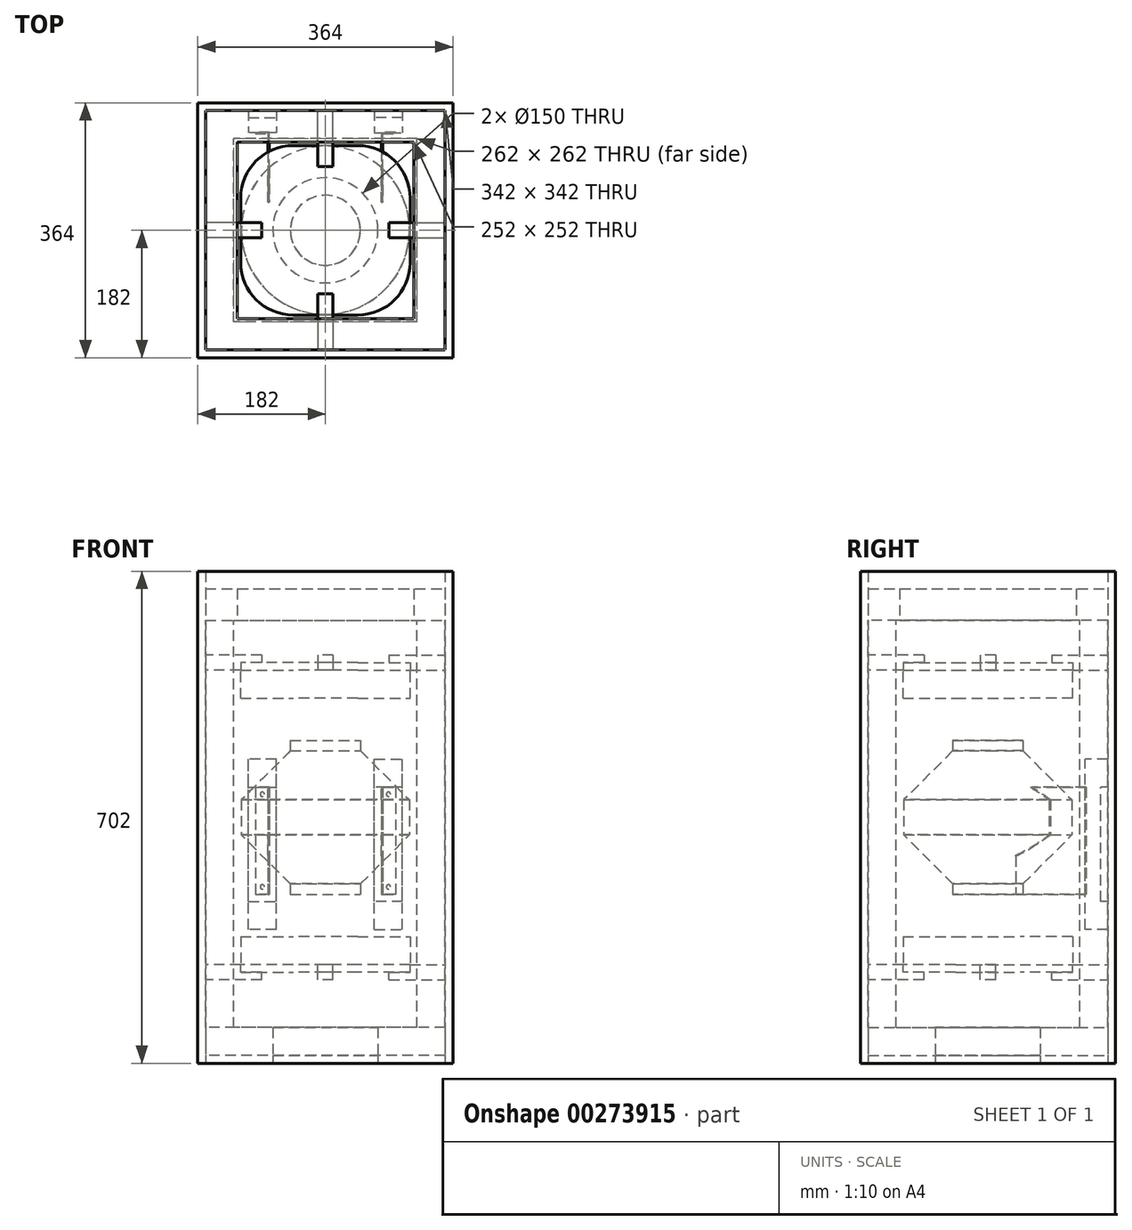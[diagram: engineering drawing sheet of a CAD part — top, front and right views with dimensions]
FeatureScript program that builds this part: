
annotation { "Feature Type Name" : "Feature", "Feature Type Description" : "" }
export const myFeature = defineFeature(function(context is Context, id is Id, definition is map)
    precondition{}
    {
        {
            assignVariable(context, id + "F0", {"variableType" : VariableType.LENGTH, "name" : "FanHeight", "lengthValue" : 220 * mm});
        }
        {
            assignVariable(context, id + "F1", {"variableType" : VariableType.LENGTH, "name" : "DistToPlate", "lengthValue" : 100 * mm});
        }
        {
            assignVariable(context, id + "F2", {"variableType" : VariableType.LENGTH, "name" : "InsulThickness", "lengthValue" : 40 * mm});
        }
        {
            var Q0;
            Q0=qCreatedBy(makeId("Front.planeOp"),FACE);
            var sketch = newSketch(context, id + "F3", { "sketchPlane" : qUnion([Q0])});
            skLineSegment(sketch, "E0", {"start": v(0, 110) * mm, "end": v(-50, 110) * mm});
            skLineSegment(sketch, "E1", {"start": v(-50, 110) * mm, "end": v(-50, 95) * mm});
            skLineSegment(sketch, "E2", {"start": v(-50, 95) * mm, "end": v(-120, 25) * mm});
            skLineSegment(sketch, "E3", {"start": v(-120, 25) * mm, "end": v(-120, -25) * mm});
            skLineSegment(sketch, "E4", {"start": v(-120, -25) * mm, "end": v(-50, -95) * mm});
            skLineSegment(sketch, "E5", {"start": v(-50, -95) * mm, "end": v(-50, -110) * mm});
            skLineSegment(sketch, "E6", {"start": v(-50, -110) * mm, "end": v(0, -110) * mm});
            skLineSegment(sketch, "E7", {"start": v(0, -110) * mm, "end": v(0, 110) * mm});
            skSolve(sketch);
        }
        {
            var Q0;
            Q0=qSketchRegion(id+"F3",true);
            var Q1;
            Q1=sQuery(id+"F3.wireOp",EDGE,"E7");
            revolve(context, id + "F4", {"surfaceOperationType" : NewSurfaceOperationType.NEW, "entities" : qUnion([Q0]), "axis" : qUnion([Q1]), "revolveType" : RevolveType.FULL});
        }
        {
            var Q0;
            Q0=qCreatedBy(makeId("Top.planeOp"),FACE);
            cPlane(context, id + "F5", {"entities" : qUnion([Q0]), "cplaneType" : CPlaneType.OFFSET, "offset" : (getVariable(context, 'FanHeight') / 2), "oppositeDirection" : true, "width" : 150 * mm, "height" : 150 * mm});
        }
        {
            var Q0;
            Q0=qCreatedBy(id+"F5.planeOp",FACE);
            var sketch = newSketch(context, id + "F6", { "sketchPlane" : qUnion([Q0])});
            skLineSegment(sketch, "E8", {"start": v(82, 40) * mm, "end": v(82, 138) * mm});
            skLineSegment(sketch, "E9", {"start": v(82, 138) * mm, "end": v(100, 138) * mm});
            skLineSegment(sketch, "E10", {"start": v(100, 138) * mm, "end": v(100, 140) * mm});
            skLineSegment(sketch, "E11", {"start": v(100, 140) * mm, "end": v(80, 140) * mm});
            skLineSegment(sketch, "E12", {"start": v(80, 140) * mm, "end": v(80, 40) * mm});
            skLineSegment(sketch, "E13", {"start": v(80, 40) * mm, "end": v(82, 40) * mm});
            skLineSegment(sketch, "E14", {"start": v(-80, 40) * mm, "end": v(-80, 140) * mm});
            skLineSegment(sketch, "E15", {"start": v(-80, 140) * mm, "end": v(-100, 140) * mm});
            skLineSegment(sketch, "E16", {"start": v(-100, 140) * mm, "end": v(-100, 138) * mm});
            skLineSegment(sketch, "E17", {"start": v(-100, 138) * mm, "end": v(-82, 138) * mm});
            skLineSegment(sketch, "E18", {"start": v(-82, 138) * mm, "end": v(-82, 40) * mm});
            skLineSegment(sketch, "E19", {"start": v(-82, 40) * mm, "end": v(-80, 40) * mm});
            skSolve(sketch);
        }
        {
            var Q0;
            Q0=qSketchRegion(id+"F6",true);
            extrude(context, id + "F7", {"entities" : qUnion([Q0]), "operationType" : NewBodyOperationType.ADD, "offsetDistance" : 25 * mm, "depth" : 153 * mm});
        }
        {
            var Q0;
            Q0=makeQuery(id+"F7.opExtrude","SWEPT_FACE",FACE,{"disambiguationData":[OSD([sQuery(id+"F6.wireOp",EDGE,"E11")])]});
            var sketch = newSketch(context, id + "F8", { "sketchPlane" : qUnion([Q0])});
            skCircle(sketch, "E20", {"center": v(-90, 33) * mm, "radius": 3 * mm});
            skCircle(sketch, "E21", {"center": v(-90, -99.22) * mm, "radius": 3 * mm});
            skCircle(sketch, "E22", {"center": v(90, -99.22) * mm, "radius": 3 * mm});
            skCircle(sketch, "E23", {"center": v(90, 33) * mm, "radius": 3 * mm});
            skLineSegment(sketch, "E24", {"start": v(-90, 43) * mm, "end": v(-90, -69.24) * mm, "construction": true});
            skPoint(sketch, "E24.endSnap0", {"position": v(-90, 43) * mm});
            skPoint(sketch, "E25", {"position": v(-90, -110) * mm});
            skSolve(sketch);
        }
        {
            var Q0;
            Q0=qSketchRegion(id+"F8",true);
            extrude(context, id + "F9", {"entities" : qUnion([Q0]), "operationType" : NewBodyOperationType.REMOVE, "oppositeDirection" : true, "offsetDistance" : 25 * mm, "depth" : 25 * mm});
        }
        {
            var Q0;
            Q0=makeQuery(id+"F7.opExtrude","SWEPT_FACE",FACE,{"disambiguationData":[OSD([sQuery(id+"F6.wireOp",EDGE,"E11")])]});
            var Q1;
            Q1=makeQuery(id+"F7.opExtrude","SWEPT_FACE",FACE,{"disambiguationData":[OSD([sQuery(id+"F6.wireOp",EDGE,"E9")])]});
            cPlane(context, id + "F10", {"entities" : qUnion([Q0, Q1]), "cplaneType" : CPlaneType.MID_PLANE, "offset" : 25 * mm, "width" : 150 * mm, "height" : 150 * mm});
        }
        {
            var Q0;
            Q0=qCreatedBy(id+"F10.planeOp",FACE);
            var sketch = newSketch(context, id + "F11", { "sketchPlane" : qUnion([Q0])});
            skCircle(sketch, "E26.0", {"center": v(-90, 33) * mm, "radius": 3 * mm, "construction": true});
            skLineSegment(sketch, "E27.bottom", {"start": v(-70, -160) * mm, "end": v(-110, -160) * mm});
            skLineSegment(sketch, "E27.top", {"start": v(-70, 83) * mm, "end": v(-110, 83) * mm});
            skLineSegment(sketch, "E27.left", {"start": v(-70, -160) * mm, "end": v(-70, 83) * mm});
            skLineSegment(sketch, "E27.right", {"start": v(-110, -160) * mm, "end": v(-110, 83) * mm});
            skPoint(sketch, "E27.middle", {"position": v(-90, -38.5) * mm});
            skSolve(sketch);
        }
        {
            var Q0;
            Q0 = qSketchRegion(id + "F11", true);
            extrude(context, id + "F12", {"entities" : qUnion([Q0]), "depth" : 22 * mm, "offsetDistance" : 25 * mm});
        }
        {
            var Q0;
            Q0=makeQuery(id+"F12.opExtrude","CAP_FACE",FACE,{"disambiguationData":[OSD([sQuery(id+"F11.wireOp",EDGE,"E27.bottom"),sQuery(id+"F11.wireOp",EDGE,"E27.top"),sQuery(id+"F11.wireOp",EDGE,"E27.left"),sQuery(id+"F11.wireOp",EDGE,"E27.right")])],"isStart":false});
            var sketch = newSketch(context, id + "F13", { "sketchPlane" : qUnion([Q0])});
            skLineSegment(sketch, "E28.bottom", {"start": v(-110, 83) * mm, "end": v(-70, 83) * mm});
            skLineSegment(sketch, "E28.top", {"start": v(-110, 43) * mm, "end": v(-70, 43) * mm});
            skLineSegment(sketch, "E28.left", {"start": v(-110, 83) * mm, "end": v(-110, 43) * mm});
            skLineSegment(sketch, "E28.right", {"start": v(-70, 83) * mm, "end": v(-70, 43) * mm});
            skLineSegment(sketch, "E29.bottom", {"start": v(-110, -160) * mm, "end": v(-70, -160) * mm});
            skLineSegment(sketch, "E29.top", {"start": v(-110, -120) * mm, "end": v(-70, -120) * mm});
            skLineSegment(sketch, "E29.left", {"start": v(-110, -160) * mm, "end": v(-110, -120) * mm});
            skLineSegment(sketch, "E29.right", {"start": v(-70, -160) * mm, "end": v(-70, -120) * mm});
            skSolve(sketch);
        }
        {
            var Q0;
            Q0 = qSketchRegion(id + "F13", true);
            extrude(context, id + "F14", {"entities" : qUnion([Q0]), "operationType" : NewBodyOperationType.ADD, "depth" : 10 * mm, "offsetDistance" : 25 * mm});
        }
        {
            var Q0;
            Q0=makeQuery(id+"F12.opExtrude","SWEPT_BODY",BODY,{"disambiguationData":[OSD([sQuery(id+"F11.wireOp",EDGE,"E27.bottom"),sQuery(id+"F11.wireOp",EDGE,"E27.top"),sQuery(id+"F11.wireOp",EDGE,"E27.left"),sQuery(id+"F11.wireOp",EDGE,"E27.right")])]});
            var Q1;
            Q1=qCreatedBy(makeId("Right.planeOp"),FACE);
            mirror(context, id + "F15", {"entities" : qUnion([Q0]), "mirrorPlane" : qUnion([Q1])});
        }
        {
            var Q0;
            Q0=qCreatedBy(makeId("Top.planeOp"),FACE);
            cPlane(context, id + "F16", {"entities" : qUnion([Q0]), "cplaneType" : CPlaneType.OFFSET, "offset" : (getVariable(context, 'FanHeight') / 2 + getVariable(context, 'DistToPlate')), "width" : 150 * mm, "height" : 150 * mm});
        }
        {
            var Q0;
            Q0=qCreatedBy(id+"F16.planeOp",FACE);
            var sketch = newSketch(context, id + "F17", { "sketchPlane" : qUnion([Q0])});
            skLineSegment(sketch, "E30.bottom", {"start": v(121, -121) * mm, "end": v(-121, -121) * mm});
            skLineSegment(sketch, "E30.top", {"start": v(121, 121) * mm, "end": v(-121, 121) * mm});
            skLineSegment(sketch, "E30.left", {"start": v(121, -121) * mm, "end": v(121, 121) * mm});
            skLineSegment(sketch, "E30.right", {"start": v(-121, -121) * mm, "end": v(-121, 121) * mm});
            skPoint(sketch, "E30.middle", {"position": v(0, 0) * mm});
            skSolve(sketch);
        }
        {
            var Q0;
            Q0 = qSketchRegion(id + "F17", true);
            extrude(context, id + "F18", {"entities" : qUnion([Q0]), "depth" : 11 * mm, "offsetDistance" : 25 * mm});
        }
        {
            var Q0;
            Q0=makeQuery(id+"F18.opExtrude","CAP_FACE",FACE,{"disambiguationData":[OSD([sQuery(id+"F17.wireOp",EDGE,"E30.bottom"),sQuery(id+"F17.wireOp",EDGE,"E30.top"),sQuery(id+"F17.wireOp",EDGE,"E30.left"),sQuery(id+"F17.wireOp",EDGE,"E30.right")])],"isStart":true});
            var sketch = newSketch(context, id + "F19", { "sketchPlane" : qUnion([Q0])});
            skLineSegment(sketch, "E31.bottom", {"start": v(171, -171) * mm, "end": v(-171, -171) * mm, "construction": true});
            skLineSegment(sketch, "E31.top", {"start": v(171, 171) * mm, "end": v(-171, 171) * mm, "construction": true});
            skLineSegment(sketch, "E31.left", {"start": v(171, -171) * mm, "end": v(171, 171) * mm, "construction": true});
            skLineSegment(sketch, "E31.right", {"start": v(-171, -171) * mm, "end": v(-171, 171) * mm, "construction": true});
            skPoint(sketch, "E31.middle", {"position": v(0, 0) * mm});
            skLineSegment(sketch, "E32.bottom", {"start": v(-91, -11) * mm, "end": v(-171, -11) * mm});
            skLineSegment(sketch, "E32.top", {"start": v(-91, 11) * mm, "end": v(-171, 11) * mm});
            skLineSegment(sketch, "E32.left", {"start": v(-91, -11) * mm, "end": v(-91, 11) * mm});
            skLineSegment(sketch, "E32.right", {"start": v(-171, -11) * mm, "end": v(-171, 11) * mm});
            skPoint(sketch, "E32.middle", {"position": v(-131, 0) * mm});
            skSolve(sketch);
        }
        {
            var Q0;
            Q0 = qSketchRegion(id + "F19", true);
            extrude(context, id + "F20", {"entities" : qUnion([Q0]), "oppositeDirection" : true, "depth" : 22 * mm, "offsetDistance" : 25 * mm});
        }
        {
            var Q0;
            Q0=makeQuery(id+"F18.opExtrude","SWEPT_BODY",BODY,{"disambiguationData":[OSD([sQuery(id+"F17.wireOp",EDGE,"E30.bottom"),sQuery(id+"F17.wireOp",EDGE,"E30.top"),sQuery(id+"F17.wireOp",EDGE,"E30.left"),sQuery(id+"F17.wireOp",EDGE,"E30.right")])]});
            var Q1;
            Q1=makeQuery(id+"F20.opExtrude","SWEPT_BODY",BODY,{"disambiguationData":[OSD([sQuery(id+"F19.wireOp",EDGE,"E32.bottom"),sQuery(id+"F19.wireOp",EDGE,"E32.top"),sQuery(id+"F19.wireOp",EDGE,"E32.left"),sQuery(id+"F19.wireOp",EDGE,"E32.right")])]});
            booleanBodies(context, id + "F21", {"operationType" : BooleanOperationType.SUBTRACTION, "tools" : qUnion([Q0]), "targets" : qUnion([Q1]), "keepTools" : true});
        }
        {
            var Q0;
            Q0=makeQuery(id+"F18.opExtrude","SWEPT_EDGE",EDGE,{"disambiguationData":[OSD([sQuery(id+"F17.wireOp",EDGE,"E30.top"),sQuery(id+"F17.wireOp",EDGE,"E30.right")])]});
            var Q1;
            Q1=makeQuery(id+"F18.opExtrude","SWEPT_EDGE",EDGE,{"disambiguationData":[OSD([sQuery(id+"F17.wireOp",EDGE,"E30.top"),sQuery(id+"F17.wireOp",EDGE,"E30.left")])]});
            var Q2;
            Q2=makeQuery(id+"F18.opExtrude","SWEPT_EDGE",EDGE,{"disambiguationData":[OSD([sQuery(id+"F17.wireOp",EDGE,"E30.bottom"),sQuery(id+"F17.wireOp",EDGE,"E30.right")])]});
            var Q3;
            Q3=makeQuery(id+"F18.opExtrude","SWEPT_EDGE",EDGE,{"disambiguationData":[OSD([sQuery(id+"F17.wireOp",EDGE,"E30.bottom"),sQuery(id+"F17.wireOp",EDGE,"E30.left")])]});
            fillet(context, id + "F22", {"entities" : qUnion([Q0, Q1, Q2, Q3]), "tangentPropagation" : true, "radius" : 75 * mm, "defaultsChanged" : true, "vertexSettings" : [], "allowEdgeOverflow" : false});
        }
        {
            var Q0;
            Q0=makeQuery(id+"F20.opExtrude","SWEPT_BODY",BODY,{"disambiguationData":[OSD([sQuery(id+"F19.wireOp",EDGE,"E32.bottom"),sQuery(id+"F19.wireOp",EDGE,"E32.top"),sQuery(id+"F19.wireOp",EDGE,"E32.left"),sQuery(id+"F19.wireOp",EDGE,"E32.right")])]});
            var Q1;
            Q1=makeQuery(id+"F4.opRevolve","SWEPT_EDGE",EDGE,{"disambiguationData":[OSD([sQuery(id+"F3.wireOp",EDGE,"E5"),sQuery(id+"F3.wireOp",EDGE,"E6")])]});
            circularPattern(context, id + "F23", {"entities" : qUnion([Q0]), "axis" : qUnion([Q1]), "angle" : 360 * degree, "instanceCount" : 4, "equalSpace" : true});
        }
        {
            var Q0;
            Q0=makeQuery(id+"F18.opExtrude","CAP_FACE",FACE,{"disambiguationData":[OSD([sQuery(id+"F17.wireOp",EDGE,"E30.bottom"),sQuery(id+"F17.wireOp",EDGE,"E30.top"),sQuery(id+"F17.wireOp",EDGE,"E30.left"),sQuery(id+"F17.wireOp",EDGE,"E30.right")])],"isStart":true});
            var sketch = newSketch(context, id + "F24", { "sketchPlane" : qUnion([Q0])});
            skLineSegment(sketch, "E33.0.0", {"start": v(-46, -121) * mm, "end": v(46, -121) * mm});
            skArc(sketch, "E33.0.1", {"start": v(46, -121) * mm, "mid": v(99.03, -99.03) * mm, "end": v(121, -46) * mm});
            skLineSegment(sketch, "E33.0.2", {"start": v(121, -46) * mm, "end": v(121, 46) * mm});
            skArc(sketch, "E33.0.3", {"start": v(121, 46) * mm, "mid": v(99.03, 99.03) * mm, "end": v(46, 121) * mm});
            skLineSegment(sketch, "E33.0.4", {"start": v(46, 121) * mm, "end": v(-46, 121) * mm});
            skArc(sketch, "E33.0.5", {"start": v(-46, 121) * mm, "mid": v(-99.03, 99.03) * mm, "end": v(-121, 46) * mm});
            skLineSegment(sketch, "E33.0.6", {"start": v(-121, 46) * mm, "end": v(-121, -46) * mm});
            skArc(sketch, "E33.0.7", {"start": v(-121, -46) * mm, "mid": v(-99.03, -99.03) * mm, "end": v(-46, -121) * mm});
            skSolve(sketch);
        }
        {
            var Q0;
            Q0 = qSketchRegion(id + "F24", true);
            extrude(context, id + "F25", {"entities" : qUnion([Q0]), "depth" : getVariable(context, 'InsulThickness'), "offsetDistance" : 25 * mm});
        }
        {
            var Q0;
            Q0=makeQuery(id+"F18.opExtrude","SWEPT_BODY",BODY,{"disambiguationData":[OSD([sQuery(id+"F17.wireOp",EDGE,"E30.bottom"),sQuery(id+"F17.wireOp",EDGE,"E30.top"),sQuery(id+"F17.wireOp",EDGE,"E30.left"),sQuery(id+"F17.wireOp",EDGE,"E30.right")])]});
            var Q1;
            Q1=makeQuery(id+"F20.opExtrude","SWEPT_BODY",BODY,{"disambiguationData":[OSD([sQuery(id+"F19.wireOp",EDGE,"E32.bottom"),sQuery(id+"F19.wireOp",EDGE,"E32.top"),sQuery(id+"F19.wireOp",EDGE,"E32.left"),sQuery(id+"F19.wireOp",EDGE,"E32.right")])]});
            var Q2;
            Q2=makeQuery(id+"F23.opPattern","COPY",BODY,{"derivedFrom":makeQuery(id+"F20.opExtrude","SWEPT_BODY",BODY,{"disambiguationData":[OSD([sQuery(id+"F19.wireOp",EDGE,"E32.bottom"),sQuery(id+"F19.wireOp",EDGE,"E32.top"),sQuery(id+"F19.wireOp",EDGE,"E32.left"),sQuery(id+"F19.wireOp",EDGE,"E32.right")])]}),"instanceName":"3"});
            var Q3;
            Q3=makeQuery(id+"F23.opPattern","COPY",BODY,{"derivedFrom":makeQuery(id+"F20.opExtrude","SWEPT_BODY",BODY,{"disambiguationData":[OSD([sQuery(id+"F19.wireOp",EDGE,"E32.bottom"),sQuery(id+"F19.wireOp",EDGE,"E32.top"),sQuery(id+"F19.wireOp",EDGE,"E32.left"),sQuery(id+"F19.wireOp",EDGE,"E32.right")])]}),"instanceName":"2"});
            var Q4;
            Q4=makeQuery(id+"F23.opPattern","COPY",BODY,{"derivedFrom":makeQuery(id+"F20.opExtrude","SWEPT_BODY",BODY,{"disambiguationData":[OSD([sQuery(id+"F19.wireOp",EDGE,"E32.bottom"),sQuery(id+"F19.wireOp",EDGE,"E32.top"),sQuery(id+"F19.wireOp",EDGE,"E32.left"),sQuery(id+"F19.wireOp",EDGE,"E32.right")])]}),"instanceName":"1"});
            var Q5;
            Q5=makeQuery(id+"F25.opExtrude","SWEPT_BODY",BODY,{"disambiguationData":[OSD([sQuery(id+"F24.wireOp",EDGE,"E33.0.0"),sQuery(id+"F24.wireOp",EDGE,"E33.0.1"),sQuery(id+"F24.wireOp",EDGE,"E33.0.2"),sQuery(id+"F24.wireOp",EDGE,"E33.0.3"),sQuery(id+"F24.wireOp",EDGE,"E33.0.4"),sQuery(id+"F24.wireOp",EDGE,"E33.0.5"),sQuery(id+"F24.wireOp",EDGE,"E33.0.6"),sQuery(id+"F24.wireOp",EDGE,"E33.0.7")])]});
            var Q6;
            Q6=qCreatedBy(makeId("Top.planeOp"),FACE);
            mirror(context, id + "F26", {"entities" : qUnion([Q0, Q1, Q2, Q3, Q4, Q5]), "mirrorPlane" : qUnion([Q6])});
        }
        {
            var Q0;
            Q0=qCreatedBy(makeId("Top.planeOp"),FACE);
            var sketch = newSketch(context, id + "F27", { "sketchPlane" : qUnion([Q0])});
            skLineSegment(sketch, "E34.bottom", {"start": v(171, -171) * mm, "end": v(-171, -171) * mm});
            skLineSegment(sketch, "E34.top", {"start": v(171, 171) * mm, "end": v(-171, 171) * mm});
            skLineSegment(sketch, "E34.left", {"start": v(171, -171) * mm, "end": v(171, 171) * mm});
            skLineSegment(sketch, "E34.right", {"start": v(-171, -171) * mm, "end": v(-171, 171) * mm});
            skPoint(sketch, "E34.middle", {"position": v(0, 0) * mm});
            skLineSegment(sketch, "E35.bottom", {"start": v(182, -182) * mm, "end": v(-182, -182) * mm});
            skLineSegment(sketch, "E35.top", {"start": v(182, 182) * mm, "end": v(-182, 182) * mm});
            skLineSegment(sketch, "E35.left", {"start": v(182, -182) * mm, "end": v(182, 182) * mm});
            skLineSegment(sketch, "E35.right", {"start": v(-182, -182) * mm, "end": v(-182, 182) * mm});
            skSolve(sketch);
        }
        {
            var Q0;
            Q0 = qSketchRegion(id + "F27", true);
            extrude(context, id + "F28", {"entities" : qUnion([Q0]), "endBound" : BoundingType.SYMMETRIC, "depth" : getVariable(context, 'FanHeight') + getVariable(context, 'DistToPlate') * 4 + 11 * 2 * mm + 20 * mm + 40 * mm, "offsetDistance" : 25 * mm});
        }
        {
            var Q0;
            Q0=makeQuery(id+"F28.opExtrude","CAP_FACE",FACE,{"disambiguationData":[OSD([sQuery(id+"F27.wireOp",EDGE,"E34.bottom"),sQuery(id+"F27.wireOp",EDGE,"E34.top"),sQuery(id+"F27.wireOp",EDGE,"E34.left"),sQuery(id+"F27.wireOp",EDGE,"E34.right"),sQuery(id+"F27.wireOp",EDGE,"E35.bottom"),sQuery(id+"F27.wireOp",EDGE,"E35.top"),sQuery(id+"F27.wireOp",EDGE,"E35.left"),sQuery(id+"F27.wireOp",EDGE,"E35.right")])],"isStart":true});
            var sketch = newSketch(context, id + "F29", { "sketchPlane" : qUnion([Q0])});
            skLineSegment(sketch, "E36.bottom", {"start": v(171, -171) * mm, "end": v(-171, -171) * mm});
            skLineSegment(sketch, "E36.top", {"start": v(171, 171) * mm, "end": v(-171, 171) * mm});
            skLineSegment(sketch, "E36.left", {"start": v(171, -171) * mm, "end": v(171, 171) * mm});
            skLineSegment(sketch, "E36.right", {"start": v(-171, -171) * mm, "end": v(-171, 171) * mm});
            skPoint(sketch, "E36.middle", {"position": v(0, 0) * mm});
            skCircle(sketch, "E37", {"center": v(0, 0) * mm, "radius": 75 * mm});
            skSolve(sketch);
        }
        {
            var Q0;
            Q0 = qSketchRegion(id + "F29", true);
            extrude(context, id + "F30", {"entities" : qUnion([Q0]), "oppositeDirection" : true, "depth" : 11 * mm, "offsetDistance" : 25 * mm});
        }
        {
            var Q0;
            Q0=makeQuery(id+"F30.opExtrude","CAP_FACE",FACE,{"disambiguationData":[OSD([sQuery(id+"F29.wireOp",EDGE,"E36.bottom"),sQuery(id+"F29.wireOp",EDGE,"E36.top"),sQuery(id+"F29.wireOp",EDGE,"E36.left"),sQuery(id+"F29.wireOp",EDGE,"E36.right"),sQuery(id+"F29.wireOp",EDGE,"E37")])],"isStart":false});
            var sketch = newSketch(context, id + "F31", { "sketchPlane" : qUnion([Q0])});
            skLineSegment(sketch, "E38.0.0", {"start": v(171, 171) * mm, "end": v(-171, 171) * mm});
            skLineSegment(sketch, "E38.0.1", {"start": v(-171, 171) * mm, "end": v(-171, -171) * mm});
            skLineSegment(sketch, "E38.0.2", {"start": v(-171, -171) * mm, "end": v(171, -171) * mm});
            skLineSegment(sketch, "E38.0.3", {"start": v(171, -171) * mm, "end": v(171, 171) * mm});
            skCircle(sketch, "E39.0", {"center": v(0, 0) * mm, "radius": 75 * mm});
            skSolve(sketch);
        }
        {
            var Q0;
            Q0 = qSketchRegion(id + "F31", true);
            extrude(context, id + "F32", {"entities" : qUnion([Q0]), "depth" : getVariable(context, 'InsulThickness'), "offsetDistance" : 25 * mm});
        }
        {
            var Q0;
            Q0=makeQuery(id+"F28.opExtrude","CAP_FACE",FACE,{"disambiguationData":[OSD([sQuery(id+"F27.wireOp",EDGE,"E34.bottom"),sQuery(id+"F27.wireOp",EDGE,"E34.top"),sQuery(id+"F27.wireOp",EDGE,"E34.left"),sQuery(id+"F27.wireOp",EDGE,"E34.right"),sQuery(id+"F27.wireOp",EDGE,"E35.bottom"),sQuery(id+"F27.wireOp",EDGE,"E35.top"),sQuery(id+"F27.wireOp",EDGE,"E35.left"),sQuery(id+"F27.wireOp",EDGE,"E35.right")])],"isStart":false});
            cPlane(context, id + "F33", {"entities" : qUnion([Q0]), "cplaneType" : CPlaneType.OFFSET, "offset" : 70 * mm, "oppositeDirection" : true, "width" : 150 * mm, "height" : 150 * mm});
        }
        {
            var Q0;
            Q0=qCreatedBy(id+"F33.planeOp",FACE);
            var sketch = newSketch(context, id + "F34", { "sketchPlane" : qUnion([Q0])});
            skLineSegment(sketch, "E40.bottom", {"start": v(-171, -171) * mm, "end": v(171, -171) * mm});
            skLineSegment(sketch, "E40.top", {"start": v(-171, 171) * mm, "end": v(171, 171) * mm});
            skLineSegment(sketch, "E40.left", {"start": v(-171, -171) * mm, "end": v(-171, 171) * mm});
            skLineSegment(sketch, "E40.right", {"start": v(171, -171) * mm, "end": v(171, 171) * mm});
            skPoint(sketch, "E40.middle", {"position": v(0, 0) * mm});
            skLineSegment(sketch, "E41.bottom", {"start": v(-126, -126) * mm, "end": v(126, -126) * mm});
            skLineSegment(sketch, "E41.top", {"start": v(-126, 126) * mm, "end": v(126, 126) * mm});
            skLineSegment(sketch, "E41.left", {"start": v(-126, -126) * mm, "end": v(-126, 126) * mm});
            skLineSegment(sketch, "E41.right", {"start": v(126, -126) * mm, "end": v(126, 126) * mm});
            skSolve(sketch);
        }
        {
            var Q0;
            Q0 = qSketchRegion(id + "F34", true);
            extrude(context, id + "F35", {"entities" : qUnion([Q0]), "depth" : 45 * mm, "offsetDistance" : 25 * mm});
        }
        {
            var Q0;
            Q0=qCreatedBy(id+"F33.planeOp",FACE);
            var sketch = newSketch(context, id + "F36", { "sketchPlane" : qUnion([Q0])});
            skLineSegment(sketch, "E42.bottom", {"start": v(-171, 171) * mm, "end": v(171, 171) * mm});
            skLineSegment(sketch, "E42.top", {"start": v(-171, -171) * mm, "end": v(171, -171) * mm});
            skLineSegment(sketch, "E42.left", {"start": v(-171, 171) * mm, "end": v(-171, -171) * mm});
            skLineSegment(sketch, "E42.right", {"start": v(171, 171) * mm, "end": v(171, -171) * mm});
            skPoint(sketch, "E42.middle", {"position": v(0, 0) * mm});
            skLineSegment(sketch, "E43.bottom", {"start": v(-131, 131) * mm, "end": v(131, 131) * mm});
            skLineSegment(sketch, "E43.top", {"start": v(-131, -131) * mm, "end": v(131, -131) * mm});
            skLineSegment(sketch, "E43.left", {"start": v(-131, 131) * mm, "end": v(-131, -131) * mm});
            skLineSegment(sketch, "E43.right", {"start": v(131, 131) * mm, "end": v(131, -131) * mm});
            skSolve(sketch);
        }
        {
            var Q0;
            Q0=qCreatedBy(id+"F33.planeOp",FACE);
            var sketch = newSketch(context, id + "F37", { "sketchPlane" : qUnion([Q0])});
            skLineSegment(sketch, "E44.bottom", {"start": v(-171, 171) * mm, "end": v(171, 171) * mm});
            skLineSegment(sketch, "E44.top", {"start": v(-171, -171) * mm, "end": v(171, -171) * mm});
            skLineSegment(sketch, "E44.left", {"start": v(-171, 171) * mm, "end": v(-171, -171) * mm});
            skLineSegment(sketch, "E44.right", {"start": v(171, 171) * mm, "end": v(171, -171) * mm});
            skPoint(sketch, "E44.middle", {"position": v(0, 0) * mm});
            skLineSegment(sketch, "E45.bottom", {"start": v(-131, 131) * mm, "end": v(131, 131) * mm});
            skLineSegment(sketch, "E45.top", {"start": v(-131, -131) * mm, "end": v(131, -131) * mm});
            skLineSegment(sketch, "E45.left", {"start": v(-131, 131) * mm, "end": v(-131, -131) * mm});
            skLineSegment(sketch, "E45.right", {"start": v(131, 131) * mm, "end": v(131, -131) * mm});
            skSolve(sketch);
        }
        {
            var Q0;
            Q0 = qSketchRegion(id + "F37", true);
            var Q1;
            Q1=makeQuery(id+"F32.opExtrude","CAP_FACE",FACE,{"disambiguationData":[OSD([sQuery(id+"F31.wireOp",EDGE,"E38.0.0"),sQuery(id+"F31.wireOp",EDGE,"E38.0.1"),sQuery(id+"F31.wireOp",EDGE,"E38.0.2"),sQuery(id+"F31.wireOp",EDGE,"E38.0.3"),sQuery(id+"F31.wireOp",EDGE,"E39.0")])],"isStart":false});
            extrude(context, id + "F38", {"entities" : qUnion([Q0]), "endBound" : BoundingType.UP_TO_SURFACE, "oppositeDirection" : true, "depth" : 25 * mm, "endBoundEntityFace" : qUnion([Q1]), "offsetDistance" : 25 * mm});
        }
    });
